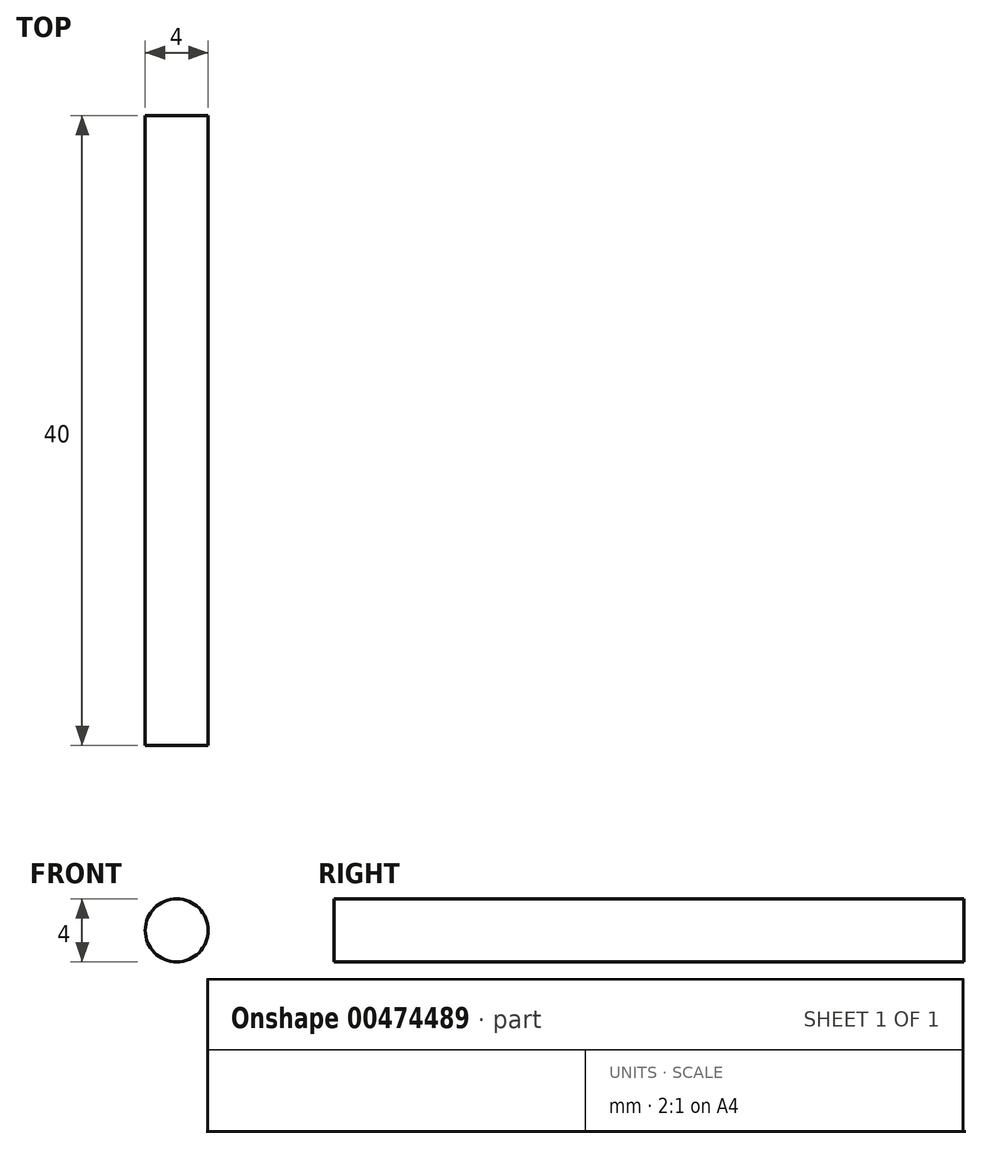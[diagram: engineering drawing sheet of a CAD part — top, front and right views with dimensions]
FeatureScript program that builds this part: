
annotation { "Feature Type Name" : "Feature", "Feature Type Description" : "" }
export const myFeature = defineFeature(function(context is Context, id is Id, definition is map)
    precondition{}
    {
        {
            var Q0;
            Q0=qCreatedBy(makeId("Top.planeOp"),FACE);
            var sketch = newSketch(context, id + "F0", { "sketchPlane" : qUnion([Q0])});
            skLineSegment(sketch, "E0.bottom", {"start": v(-1, 20) * mm, "end": v(1, 20) * mm});
            skLineSegment(sketch, "E0.top", {"start": v(-1, -20) * mm, "end": v(1, -20) * mm});
            skLineSegment(sketch, "E0.left", {"start": v(-1, 20) * mm, "end": v(-1, -20) * mm});
            skLineSegment(sketch, "E0.right", {"start": v(1, 20) * mm, "end": v(1, -20) * mm});
            skPoint(sketch, "E0.middle", {"position": v(0, 0) * mm});
            skSolve(sketch);
        }
        {
            var Q0;
            Q0 = qSketchRegion(id + "F0", true);
            var Q1;
            Q1=sQuery(id+"F0.wireOp",EDGE,"E0.left");
            revolve(context, id + "F1", {"entities" : qUnion([Q0]), "axis" : qUnion([Q1]), "revolveType" : RevolveType.FULL});
        }
    });
